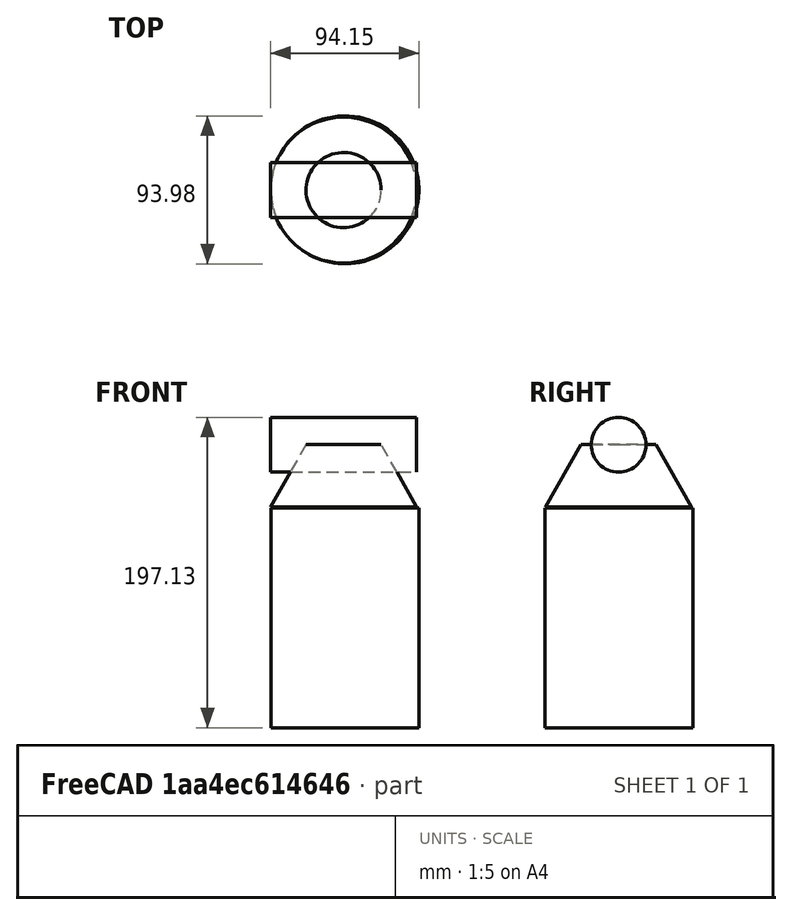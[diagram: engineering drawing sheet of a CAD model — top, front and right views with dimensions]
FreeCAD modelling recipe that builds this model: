
FCSTD DOCUMENT  (FreeCAD 0.17R11792 (Git))
Label: PC_1708_oil_filter
License: All rights reserved
LicenseURL: http://en.wikipedia.org/wiki/All_rights_reserved
objects: Part::Cylinder×2, App::MeasureDistance×2, Part::Cone×1
note: 3 computed .brp shape members not serialized (recipe doc carries the construction recipe); baked Part::Feature solids carry a one-line shape summary decoded from their .brp

FEATURE [Part::Cone] Cone
  Angle = 360
  AttacherType = Attacher::AttachEngine3D
  Height = 39.624
  Radius1 = 46.355
  Radius2 = 23.876
FEATURE [Part::Cylinder] Cylinder
  Angle = 360
  AttacherType = Attacher::AttachEngine3D
  Height = 92.71
  Placement = pos=(-46.355,0,39.624) rot=(0,1,0;1.5708rad)
  Radius = 17.399
FEATURE [Part::Cylinder] Cylinder001
  Angle = 360
  AttacherType = Attacher::AttachEngine3D
  Height = 139.7
  Placement = pos=(0.80928,0.17202,-140.113) rot=(0,0,1;0rad)
  Radius = 46.99
FEATURE [App::MeasureDistance] Distance  label="Distance: 6.95 in"
  Distance = 176.531
  P1 = (-46.8002,-1.68411,0)
  P2 = (-46.7457,-2.16865,-176.53)
FEATURE [App::MeasureDistance] Distance001  label="Distance: 3.63 in"
  Distance = 92.2631
  P1 = (-46.355,-17.2721,37.9657)
  P2 = (45.8478,-17.2721,41.301)
